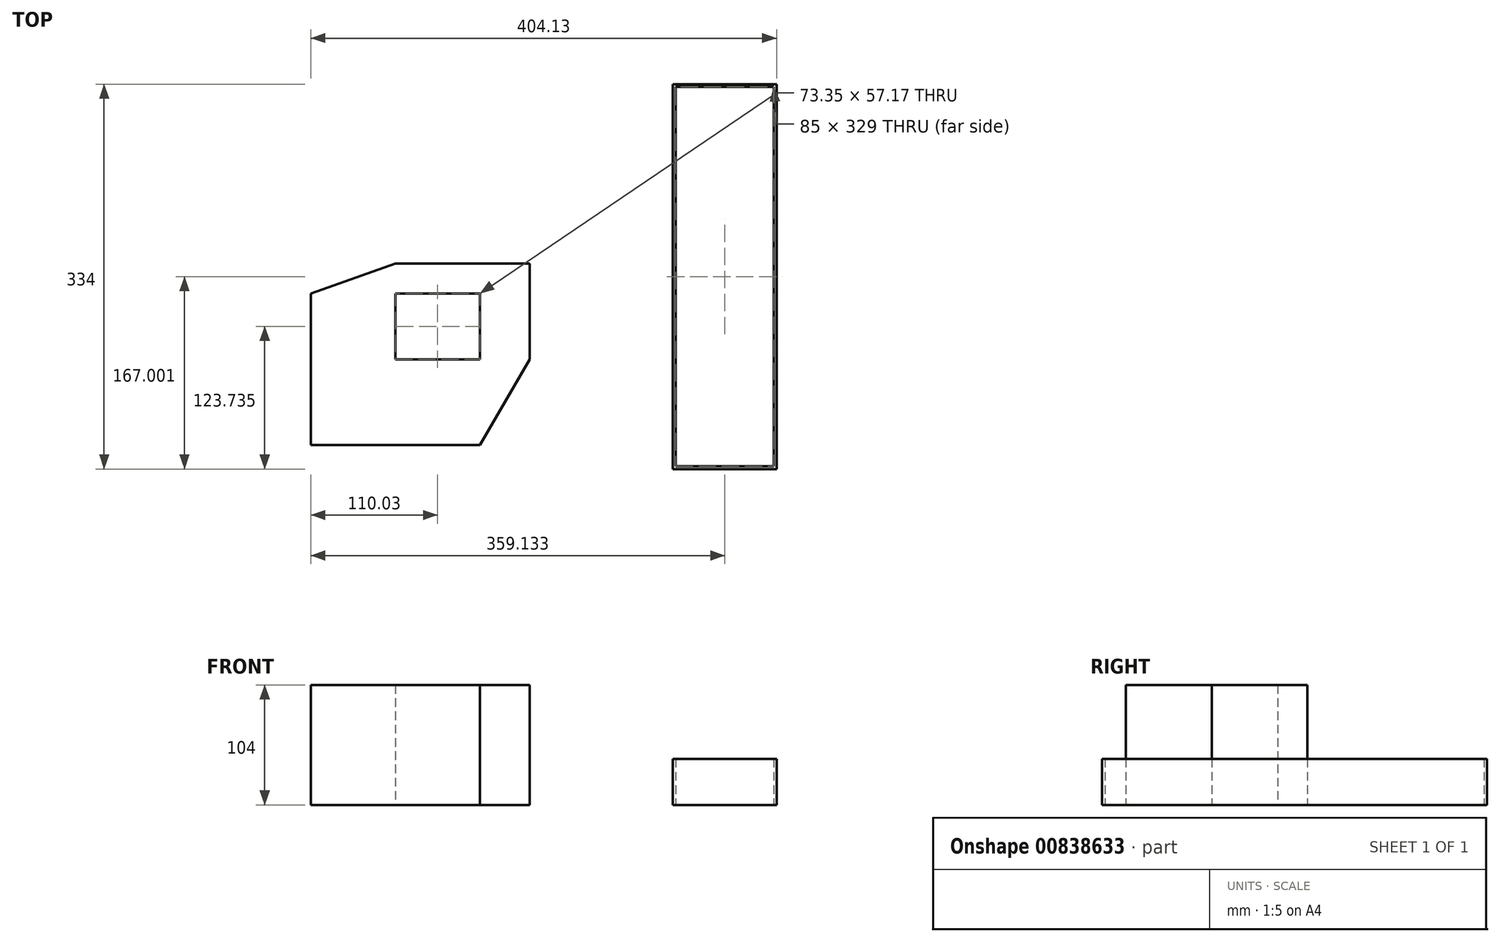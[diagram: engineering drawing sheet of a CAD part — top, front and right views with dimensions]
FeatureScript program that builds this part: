
annotation { "Feature Type Name" : "Feature", "Feature Type Description" : "" }
export const myFeature = defineFeature(function(context is Context, id is Id, definition is map)
    precondition{}
    {
        {
            var Q0;
            Q0=qCreatedBy(makeId("Top.planeOp"),FACE);
            var sketch = newSketch(context, id + "F0", { "sketchPlane" : qUnion([Q0])});
            skLineSegment(sketch, "E0.bottom", {"start": v(-43.46, 313.28) * mm, "end": v(46.54, 313.28) * mm});
            skLineSegment(sketch, "E0.top", {"start": v(-43.46, -20.72) * mm, "end": v(46.54, -20.72) * mm});
            skLineSegment(sketch, "E0.left", {"start": v(-43.46, 313.28) * mm, "end": v(-43.46, -20.72) * mm});
            skLineSegment(sketch, "E0.right", {"start": v(46.54, 313.28) * mm, "end": v(46.54, -20.72) * mm});
            skSolve(sketch);
        }
        {
            var Q0;
            Q0 = qSketchRegion(id + "F0", true);
            extrude(context, id + "F1", {"entities" : qUnion([Q0]), "depth" : 40 * mm, "offsetDistance" : 25 * mm});
        }
        {
            var Q0;
            Q0=makeQuery(id+"F1.opExtrude","CAP_FACE",FACE,{"disambiguationData":[OSD([sQuery(id+"F0.wireOp",EDGE,"E0.bottom"),sQuery(id+"F0.wireOp",EDGE,"E0.top"),sQuery(id+"F0.wireOp",EDGE,"E0.left"),sQuery(id+"F0.wireOp",EDGE,"E0.right")])],"isStart":false});
            var Q1;
            Q1=makeQuery(id+"F1.opExtrude","CAP_FACE",FACE,{"disambiguationData":[OSD([sQuery(id+"F0.wireOp",EDGE,"E0.bottom"),sQuery(id+"F0.wireOp",EDGE,"E0.top"),sQuery(id+"F0.wireOp",EDGE,"E0.left"),sQuery(id+"F0.wireOp",EDGE,"E0.right")])],"isStart":true});
            shell(context, id + "F2", {"entities" : qUnion([Q0, Q1]), "thickness" : 2.5 * mm});
        }
        {
            var Q0;
            Q0=qCreatedBy(makeId("Top.planeOp"),FACE);
            var sketch = newSketch(context, id + "F3", { "sketchPlane" : qUnion([Q0])});
            skLineSegment(sketch, "E1.bottom", {"start": v(-357.59, 131.6) * mm, "end": v(-210.88, 131.6) * mm});
            skLineSegment(sketch, "E1.top", {"start": v(-357.59, 0) * mm, "end": v(-210.88, 0) * mm});
            skLineSegment(sketch, "E1.left", {"start": v(-357.59, 131.6) * mm, "end": v(-357.59, 0) * mm});
            skLineSegment(sketch, "E1.right", {"start": v(-210.88, 131.6) * mm, "end": v(-210.88, 0) * mm});
            skPoint(sketch, "E2.firstSnap0", {"position": v(-284.24, 131.6) * mm});
            skLineSegment(sketch, "E2.bottom", {"start": v(-284.24, 157.49) * mm, "end": v(-167.74, 157.49) * mm});
            skLineSegment(sketch, "E2.top", {"start": v(-284.24, 74.43) * mm, "end": v(-167.74, 74.43) * mm});
            skLineSegment(sketch, "E2.left", {"start": v(-284.24, 157.49) * mm, "end": v(-284.24, 74.43) * mm});
            skLineSegment(sketch, "E2.right", {"start": v(-167.74, 157.49) * mm, "end": v(-167.74, 74.43) * mm});
            skLineSegment(sketch, "E3", {"start": v(-357.59, 131.6) * mm, "end": v(-284.24, 157.49) * mm});
            skLineSegment(sketch, "E4", {"start": v(-210.88, 131.6) * mm, "end": v(-167.74, 157.49) * mm});
            skLineSegment(sketch, "E5", {"start": v(-210.88, 0) * mm, "end": v(-167.74, 74.43) * mm});
            skLineSegment(sketch, "E6", {"start": v(-357.59, 0) * mm, "end": v(-284.24, 74.43) * mm});
            skSolve(sketch);
        }
        {
            var Q0;
            Q0 = qSketchRegion(id + "F3", true);
            extrude(context, id + "F4", {"entities" : qUnion([Q0]), "depth" : 104 * mm, "offsetDistance" : 25 * mm});
        }
    });
